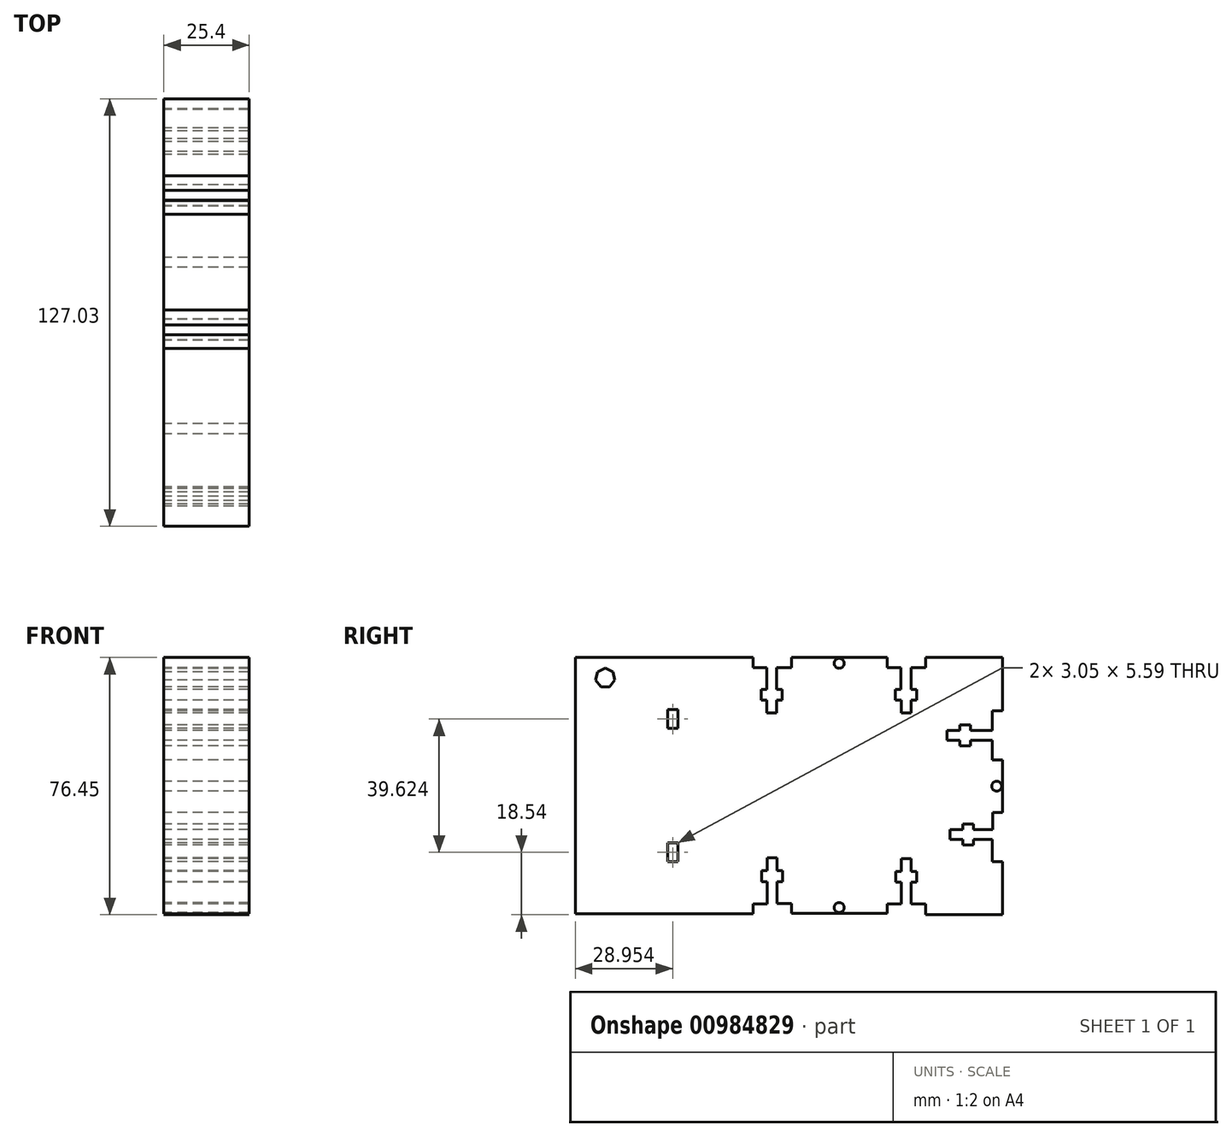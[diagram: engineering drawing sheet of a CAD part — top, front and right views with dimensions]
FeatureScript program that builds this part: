
annotation { "Feature Type Name" : "Feature", "Feature Type Description" : "" }
export const myFeature = defineFeature(function(context is Context, id is Id, definition is map)
    precondition{}
    {
        {
            var Q0;
            Q0=qCreatedBy(makeId("Right.planeOp"),FACE);
            var sketch = newSketch(context, id + "F0", { "sketchPlane" : qUnion([Q0])});
            skArc(sketch, "E0", {"start": v(-22.02, -45.03) * mm, "mid": v(-9.13, -44.74) * mm, "end": v(0.89, -36.62) * mm});
            skArc(sketch, "E1", {"start": v(18.14, -21.03) * mm, "mid": v(8.15, -27.32) * mm, "end": v(0.89, -36.62) * mm});
            skArc(sketch, "E2", {"start": v(21.6, -25.34) * mm, "mid": v(20.26, -22.87) * mm, "end": v(18.14, -21.03) * mm});
            skArc(sketch, "E3", {"start": v(21.6, -25.34) * mm, "mid": v(18.5, -36.07) * mm, "end": v(21.6, -46.8) * mm});
            skArc(sketch, "E4", {"start": v(21.6, -46.8) * mm, "mid": v(41.96, -49.62) * mm, "end": v(61.44, -43.07) * mm});
            skArc(sketch, "E5", {"start": v(68.97, -36.73) * mm, "mid": v(64.12, -38.6) * mm, "end": v(61.44, -43.07) * mm});
            skArc(sketch, "E6", {"start": v(68.97, -36.73) * mm, "mid": v(68.28, -47.93) * mm, "end": v(79.33, -49.9) * mm});
            skArc(sketch, "E7", {"start": v(112.9, -23.55) * mm, "mid": v(92.22, -31.76) * mm, "end": v(79.33, -49.9) * mm});
            skArc(sketch, "E8", {"start": v(112.9, -23.55) * mm, "mid": v(98.28, -43.41) * mm, "end": v(105.37, -67.04) * mm});
            skArc(sketch, "E9", {"start": v(105.37, -67.04) * mm, "mid": v(96.03, -62.92) * mm, "end": v(85.99, -61.04) * mm});
            skArc(sketch, "E10", {"start": v(85.99, -61.04) * mm, "mid": v(69.6, -62.3) * mm, "end": v(54.61, -69.05) * mm});
            skLineSegment(sketch, "E11", {"start": v(54.61, -69.05) * mm, "end": v(-72.39, -69.05) * mm});
            skArc(sketch, "E12", {"start": v(-22.02, -45.03) * mm, "mid": v(-51.84, -45.86) * mm, "end": v(-79.75, -56.4) * mm});
            skArc(sketch, "E13", {"start": v(-79.75, -56.4) * mm, "mid": v(-77, -61.67) * mm, "end": v(-71.28, -63.36) * mm});
            skArc(sketch, "E14", {"start": v(-48.38, -63.36) * mm, "mid": v(-59.83, -63.24) * mm, "end": v(-71.28, -63.36) * mm});
            skArc(sketch, "E15", {"start": v(-72.39, -65.62) * mm, "mid": v(-75.46, -67.33) * mm, "end": v(-72.39, -69.05) * mm});
            skArc(sketch, "E16", {"start": v(-72.39, -65.62) * mm, "mid": v(-60.25, -65.94) * mm, "end": v(-48.38, -63.36) * mm});
            skLineSegment(sketch, "E17", {"start": v(27.48, -78.47) * mm, "end": v(29.13, -78.47) * mm});
            skLineSegment(sketch, "E18", {"start": v(29.13, -78.47) * mm, "end": v(29.13, -81.72) * mm});
            skLineSegment(sketch, "E19", {"start": v(29.13, -81.72) * mm, "end": v(27.48, -81.72) * mm});
            skLineSegment(sketch, "E20", {"start": v(27.48, -81.72) * mm, "end": v(27.48, -85.53) * mm});
            skLineSegment(sketch, "E21", {"start": v(27.48, -85.53) * mm, "end": v(24.53, -85.53) * mm});
            skLineSegment(sketch, "E22", {"start": v(24.53, -85.53) * mm, "end": v(24.53, -81.72) * mm});
            skLineSegment(sketch, "E23", {"start": v(24.43, -72) * mm, "end": v(20.32, -72) * mm});
            skLineSegment(sketch, "E24", {"start": v(-44.9, -69.05) * mm, "end": v(-72.39, -69.05) * mm});
            skLineSegment(sketch, "E25", {"start": v(-72.39, -69.05) * mm, "end": v(-72.39, -145.25) * mm});
            skLineSegment(sketch, "E26", {"start": v(46.05, -123.08) * mm, "end": v(46.05, -124.73) * mm});
            skLineSegment(sketch, "E27", {"start": v(45.19, -95.3) * mm, "end": v(41.94, -95.3) * mm});
            skLineSegment(sketch, "E28", {"start": v(41.94, -95.3) * mm, "end": v(41.94, -93.65) * mm});
            skLineSegment(sketch, "E29", {"start": v(41.94, -93.65) * mm, "end": v(38.13, -93.65) * mm});
            skLineSegment(sketch, "E30", {"start": v(38.13, -93.65) * mm, "end": v(38.13, -90.7) * mm});
            skLineSegment(sketch, "E31", {"start": v(38.13, -90.7) * mm, "end": v(41.94, -90.7) * mm});
            skLineSegment(sketch, "E32", {"start": v(41.94, -90.7) * mm, "end": v(41.94, -89.05) * mm});
            skLineSegment(sketch, "E33", {"start": v(41.94, -89.05) * mm, "end": v(45.19, -89.05) * mm});
            skLineSegment(sketch, "E34", {"start": v(45.19, -89.05) * mm, "end": v(45.19, -90.7) * mm});
            skLineSegment(sketch, "E35", {"start": v(45.19, -90.7) * mm, "end": v(51.67, -90.7) * mm});
            skLineSegment(sketch, "E36", {"start": v(54.64, -115.05) * mm, "end": v(51.7, -115.05) * mm});
            skLineSegment(sketch, "E37", {"start": v(51.7, -115.05) * mm, "end": v(51.7, -120.13) * mm});
            skLineSegment(sketch, "E38", {"start": v(46.05, -120.13) * mm, "end": v(46.05, -118.48) * mm});
            skLineSegment(sketch, "E39", {"start": v(24.43, -72) * mm, "end": v(24.43, -78.47) * mm});
            skLineSegment(sketch, "E40", {"start": v(24.43, -78.47) * mm, "end": v(22.78, -78.47) * mm});
            skLineSegment(sketch, "E41", {"start": v(22.78, -78.47) * mm, "end": v(22.78, -81.72) * mm});
            skLineSegment(sketch, "E42", {"start": v(22.78, -81.72) * mm, "end": v(24.53, -81.72) * mm});
            skLineSegment(sketch, "E43", {"start": v(46.05, -118.48) * mm, "end": v(42.8, -118.48) * mm});
            skLineSegment(sketch, "E44", {"start": v(42.8, -118.48) * mm, "end": v(42.8, -120.13) * mm});
            skLineSegment(sketch, "E45", {"start": v(42.8, -120.13) * mm, "end": v(38.99, -120.13) * mm});
            skLineSegment(sketch, "E46", {"start": v(38.99, -120.13) * mm, "end": v(38.99, -123.08) * mm});
            skLineSegment(sketch, "E47", {"start": v(38.99, -123.08) * mm, "end": v(42.8, -123.08) * mm});
            skLineSegment(sketch, "E48", {"start": v(42.8, -123.08) * mm, "end": v(42.8, -124.73) * mm});
            skLineSegment(sketch, "E49", {"start": v(42.8, -124.73) * mm, "end": v(46.05, -124.73) * mm});
            skLineSegment(sketch, "E50", {"start": v(51.7, -120.13) * mm, "end": v(46.05, -120.13) * mm});
            skLineSegment(sketch, "E51", {"start": v(54.61, -129.68) * mm, "end": v(54.61, -145.5) * mm});
            skLineSegment(sketch, "E52", {"start": v(54.61, -145.5) * mm, "end": v(31.75, -145.5) * mm});
            skLineSegment(sketch, "E53", {"start": v(27.48, -78.47) * mm, "end": v(27.48, -72) * mm});
            skLineSegment(sketch, "E54", {"start": v(27.48, -72) * mm, "end": v(31.75, -72) * mm});
            skLineSegment(sketch, "E55", {"start": v(31.75, -72) * mm, "end": v(31.75, -69.05) * mm});
            skLineSegment(sketch, "E56", {"start": v(31.75, -69.05) * mm, "end": v(54.61, -69.05) * mm});
            skLineSegment(sketch, "E57", {"start": v(54.61, -69.05) * mm, "end": v(54.61, -72) * mm});
            skLineSegment(sketch, "E58", {"start": v(51.67, -84.86) * mm, "end": v(54.61, -84.86) * mm});
            skLineSegment(sketch, "E59", {"start": v(54.61, -84.86) * mm, "end": v(54.61, -72) * mm});
            skLineSegment(sketch, "E60", {"start": v(51.67, -99.48) * mm, "end": v(54.64, -99.48) * mm});
            skLineSegment(sketch, "E61", {"start": v(54.64, -99.48) * mm, "end": v(54.64, -115.05) * mm});
            skLineSegment(sketch, "E62", {"start": v(24.56, -142.32) * mm, "end": v(24.56, -135.84) * mm});
            skLineSegment(sketch, "E63", {"start": v(24.56, -135.84) * mm, "end": v(22.91, -135.84) * mm});
            skLineSegment(sketch, "E64", {"start": v(27.51, -135.84) * mm, "end": v(29.16, -135.84) * mm});
            skLineSegment(sketch, "E65", {"start": v(29.16, -135.84) * mm, "end": v(29.16, -132.59) * mm});
            skLineSegment(sketch, "E66", {"start": v(29.16, -132.59) * mm, "end": v(27.51, -132.59) * mm});
            skLineSegment(sketch, "E67", {"start": v(27.51, -132.59) * mm, "end": v(27.51, -128.78) * mm});
            skLineSegment(sketch, "E68", {"start": v(27.51, -128.78) * mm, "end": v(24.56, -128.78) * mm});
            skLineSegment(sketch, "E69", {"start": v(24.56, -128.78) * mm, "end": v(24.56, -132.59) * mm});
            skLineSegment(sketch, "E70", {"start": v(24.56, -132.59) * mm, "end": v(22.91, -132.59) * mm});
            skLineSegment(sketch, "E71", {"start": v(22.91, -132.59) * mm, "end": v(22.91, -135.84) * mm});
            skLineSegment(sketch, "E72", {"start": v(20.32, -145.07) * mm, "end": v(-8.13, -145.07) * mm});
            skLineSegment(sketch, "E73", {"start": v(-15.31, -135.65) * mm, "end": v(-16.97, -135.65) * mm});
            skLineSegment(sketch, "E74", {"start": v(-12.37, -135.65) * mm, "end": v(-10.72, -135.65) * mm});
            skLineSegment(sketch, "E75", {"start": v(-10.72, -135.65) * mm, "end": v(-10.72, -132.4) * mm});
            skLineSegment(sketch, "E76", {"start": v(-10.72, -132.4) * mm, "end": v(-12.37, -132.4) * mm});
            skLineSegment(sketch, "E77", {"start": v(-12.37, -132.4) * mm, "end": v(-12.37, -128.59) * mm});
            skLineSegment(sketch, "E78", {"start": v(-12.37, -128.59) * mm, "end": v(-15.31, -128.59) * mm});
            skLineSegment(sketch, "E79", {"start": v(-15.31, -128.59) * mm, "end": v(-15.31, -132.4) * mm});
            skLineSegment(sketch, "E80", {"start": v(-15.31, -132.4) * mm, "end": v(-16.97, -132.4) * mm});
            skLineSegment(sketch, "E81", {"start": v(-16.97, -132.4) * mm, "end": v(-16.97, -135.65) * mm});
            skLineSegment(sketch, "E82", {"start": v(-8.13, -142.12) * mm, "end": v(-8.13, -145.07) * mm});
            skLineSegment(sketch, "E83", {"start": v(-72.39, -145.25) * mm, "end": v(-19.56, -145.25) * mm});
            skLineSegment(sketch, "E84", {"start": v(20.32, -72) * mm, "end": v(20.32, -69.05) * mm});
            skLineSegment(sketch, "E85", {"start": v(20.32, -69.05) * mm, "end": v(-8.13, -69.05) * mm});
            skLineSegment(sketch, "E86", {"start": v(-8.13, -72) * mm, "end": v(-12.5, -72) * mm});
            skLineSegment(sketch, "E87", {"start": v(-12.5, -72) * mm, "end": v(-12.5, -78.47) * mm});
            skLineSegment(sketch, "E88", {"start": v(-12.5, -78.47) * mm, "end": v(-10.84, -78.47) * mm});
            skLineSegment(sketch, "E89", {"start": v(-10.84, -78.47) * mm, "end": v(-10.84, -81.72) * mm});
            skLineSegment(sketch, "E90", {"start": v(-10.84, -81.72) * mm, "end": v(-12.5, -81.72) * mm});
            skLineSegment(sketch, "E91", {"start": v(-12.5, -81.72) * mm, "end": v(-12.5, -85.53) * mm});
            skLineSegment(sketch, "E92", {"start": v(-12.5, -85.53) * mm, "end": v(-15.44, -85.53) * mm});
            skLineSegment(sketch, "E93", {"start": v(-15.44, -85.53) * mm, "end": v(-15.44, -81.72) * mm});
            skLineSegment(sketch, "E94", {"start": v(-15.44, -81.72) * mm, "end": v(-17.1, -81.72) * mm});
            skLineSegment(sketch, "E95", {"start": v(-17.1, -81.72) * mm, "end": v(-17.1, -78.47) * mm});
            skLineSegment(sketch, "E96", {"start": v(-17.1, -78.47) * mm, "end": v(-15.44, -78.47) * mm});
            skLineSegment(sketch, "E97", {"start": v(-15.44, -78.47) * mm, "end": v(-15.44, -72) * mm});
            skLineSegment(sketch, "E98", {"start": v(-15.44, -72) * mm, "end": v(-19.56, -72) * mm});
            skLineSegment(sketch, "E99", {"start": v(-19.56, -72) * mm, "end": v(-19.56, -69.05) * mm});
            skLineSegment(sketch, "E100", {"start": v(-8.13, -69.05) * mm, "end": v(-8.13, -72) * mm});
            skLineSegment(sketch, "E101", {"start": v(-44.9, -69.05) * mm, "end": v(-19.56, -69.05) * mm});
            skCircle(sketch, "E102", {"center": v(52.91, -107.27) * mm, "radius": 1.47 * mm});
            skCircle(sketch, "E103", {"center": v(6.1, -143.34) * mm, "radius": 1.47 * mm});
            skPoint(sketch, "E103.centerSnap0", {"position": v(6.1, -145.07) * mm});
            skLineSegment(sketch, "E104", {"start": v(51.64, -129.68) * mm, "end": v(54.61, -129.68) * mm});
            skLineSegment(sketch, "E105", {"start": v(46.05, -123.08) * mm, "end": v(51.65, -123.08) * mm});
            skLineSegment(sketch, "E106", {"start": v(51.65, -123.08) * mm, "end": v(51.64, -129.68) * mm});
            skLineSegment(sketch, "E107", {"start": v(54.61, -69.05) * mm, "end": v(31.75, -69.05) * mm});
            skLineSegment(sketch, "E108", {"start": v(-15.31, -135.65) * mm, "end": v(-15.31, -142.3) * mm});
            skLineSegment(sketch, "E109", {"start": v(-15.31, -142.3) * mm, "end": v(-19.56, -142.3) * mm});
            skLineSegment(sketch, "E110", {"start": v(-19.56, -142.3) * mm, "end": v(-19.56, -145.25) * mm});
            skCircle(sketch, "E111", {"center": v(6.1, -70.77) * mm, "radius": 1.47 * mm});
            skLineSegment(sketch, "E112", {"start": v(24.56, -142.32) * mm, "end": v(20.32, -142.32) * mm});
            skLineSegment(sketch, "E113", {"start": v(20.32, -142.32) * mm, "end": v(20.32, -145.07) * mm});
            skLineSegment(sketch, "E114", {"start": v(27.51, -135.84) * mm, "end": v(27.51, -142.32) * mm});
            skLineSegment(sketch, "E115", {"start": v(27.51, -142.32) * mm, "end": v(31.75, -142.32) * mm});
            skLineSegment(sketch, "E116", {"start": v(31.75, -142.32) * mm, "end": v(31.75, -145.5) * mm});
            skLineSegment(sketch, "E117", {"start": v(-12.37, -135.65) * mm, "end": v(-12.37, -142.12) * mm});
            skLineSegment(sketch, "E118", {"start": v(-12.37, -142.12) * mm, "end": v(-8.13, -142.12) * mm});
            skLineSegment(sketch, "E119", {"start": v(45.19, -95.3) * mm, "end": v(45.19, -93.64) * mm});
            skLineSegment(sketch, "E120", {"start": v(45.19, -93.64) * mm, "end": v(51.67, -93.64) * mm});
            skLineSegment(sketch, "E121", {"start": v(51.67, -93.64) * mm, "end": v(51.67, -99.48) * mm});
            skLineSegment(sketch, "E122", {"start": v(51.67, -90.7) * mm, "end": v(51.67, -84.86) * mm});
            skCircle(sketch, "E123.cCircle", {"center": v(-63.5, -75.11) * mm, "radius": 2.65 * mm, "construction": true});
            skLineSegment(sketch, "E123.0", {"start": v(-62.22, -77.77) * mm, "end": v(-64.77, -77.77) * mm});
            skLineSegment(sketch, "E123.1", {"start": v(-64.77, -77.77) * mm, "end": v(-66.36, -75.77) * mm});
            skLineSegment(sketch, "E123.2", {"start": v(-66.36, -75.77) * mm, "end": v(-65.8, -73.28) * mm});
            skLineSegment(sketch, "E123.3", {"start": v(-65.8, -73.28) * mm, "end": v(-63.5, -72.17) * mm});
            skLineSegment(sketch, "E123.4", {"start": v(-63.5, -72.17) * mm, "end": v(-61.2, -73.28) * mm});
            skLineSegment(sketch, "E123.5", {"start": v(-61.2, -73.28) * mm, "end": v(-60.62, -75.77) * mm});
            skLineSegment(sketch, "E123.6", {"start": v(-60.62, -75.77) * mm, "end": v(-62.22, -77.77) * mm});
            skPoint(sketch, "E123.0.midPoint", {"position": v(-63.5, -77.77) * mm});
            skLineSegment(sketch, "E124.bottom", {"start": v(-41.9, -84.54) * mm, "end": v(-41.9, -90.13) * mm});
            skLineSegment(sketch, "E124.top", {"start": v(-44.96, -84.54) * mm, "end": v(-44.96, -90.13) * mm});
            skLineSegment(sketch, "E124.left", {"start": v(-41.9, -84.54) * mm, "end": v(-44.96, -84.54) * mm});
            skLineSegment(sketch, "E124.right", {"start": v(-41.9, -90.13) * mm, "end": v(-44.96, -90.13) * mm});
            skLineSegment(sketch, "E125.MirrorCS", {"start": v(-41.9, -129.75) * mm, "end": v(-44.96, -129.75) * mm});
            skLineSegment(sketch, "E126.MirrorCS", {"start": v(-44.96, -129.75) * mm, "end": v(-44.96, -124.16) * mm});
            skLineSegment(sketch, "E127.MirrorCS", {"start": v(-41.9, -129.75) * mm, "end": v(-41.9, -124.16) * mm});
            skLineSegment(sketch, "E128.MirrorCS", {"start": v(-41.9, -124.16) * mm, "end": v(-44.96, -124.16) * mm});
            skSolve(sketch);
        }
        {
            var Q0;
            Q0=makeQuery(id+"F0.imprint","IMPRINT",FACE,{"disambiguationData":[TD([[makeQuery(id+"F0.imprint","IMPRINT",EDGE,{"derivedFrom":sQuery(id+"F0.wireOp",EDGE,"E17")}),1.0]])]});
            extrude(context, id + "F1", {"entities" : qUnion([Q0]), "depth" : 25.4 * mm, "offsetDistance" : 25.4 * mm});
        }
        {
            var Q0;
            Q0=makeQuery(id+"F1.opExtrude","SWEPT_BODY",BODY,{"disambiguationData":[OSD([sQuery(id+"F0.wireOp",EDGE,"E17"),sQuery(id+"F0.wireOp",EDGE,"E18"),sQuery(id+"F0.wireOp",EDGE,"E19"),sQuery(id+"F0.wireOp",EDGE,"E20"),sQuery(id+"F0.wireOp",EDGE,"E21"),sQuery(id+"F0.wireOp",EDGE,"E22"),sQuery(id+"F0.wireOp",EDGE,"E23"),sQuery(id+"F0.wireOp",EDGE,"E24"),sQuery(id+"F0.wireOp",EDGE,"E25"),sQuery(id+"F0.wireOp",EDGE,"E26"),sQuery(id+"F0.wireOp",EDGE,"E27"),sQuery(id+"F0.wireOp",EDGE,"E28"),sQuery(id+"F0.wireOp",EDGE,"E29"),sQuery(id+"F0.wireOp",EDGE,"E30"),sQuery(id+"F0.wireOp",EDGE,"E31"),sQuery(id+"F0.wireOp",EDGE,"E32"),sQuery(id+"F0.wireOp",EDGE,"E33"),sQuery(id+"F0.wireOp",EDGE,"E34"),sQuery(id+"F0.wireOp",EDGE,"E35"),sQuery(id+"F0.wireOp",EDGE,"E36"),sQuery(id+"F0.wireOp",EDGE,"E37"),sQuery(id+"F0.wireOp",EDGE,"E38"),sQuery(id+"F0.wireOp",EDGE,"E39"),sQuery(id+"F0.wireOp",EDGE,"E40"),sQuery(id+"F0.wireOp",EDGE,"E41"),sQuery(id+"F0.wireOp",EDGE,"E42"),sQuery(id+"F0.wireOp",EDGE,"E43"),sQuery(id+"F0.wireOp",EDGE,"E44"),sQuery(id+"F0.wireOp",EDGE,"E45"),sQuery(id+"F0.wireOp",EDGE,"E46"),sQuery(id+"F0.wireOp",EDGE,"E47"),sQuery(id+"F0.wireOp",EDGE,"E48"),sQuery(id+"F0.wireOp",EDGE,"E49"),sQuery(id+"F0.wireOp",EDGE,"E50"),sQuery(id+"F0.wireOp",EDGE,"E51"),sQuery(id+"F0.wireOp",EDGE,"E52"),sQuery(id+"F0.wireOp",EDGE,"E53"),sQuery(id+"F0.wireOp",EDGE,"E54"),sQuery(id+"F0.wireOp",EDGE,"E55"),sQuery(id+"F0.wireOp",EDGE,"E57"),sQuery(id+"F0.wireOp",EDGE,"E58"),sQuery(id+"F0.wireOp",EDGE,"E59"),sQuery(id+"F0.wireOp",EDGE,"E60"),sQuery(id+"F0.wireOp",EDGE,"E61"),sQuery(id+"F0.wireOp",EDGE,"E62"),sQuery(id+"F0.wireOp",EDGE,"E63"),sQuery(id+"F0.wireOp",EDGE,"E64"),sQuery(id+"F0.wireOp",EDGE,"E65"),sQuery(id+"F0.wireOp",EDGE,"E66"),sQuery(id+"F0.wireOp",EDGE,"E67"),sQuery(id+"F0.wireOp",EDGE,"E68"),sQuery(id+"F0.wireOp",EDGE,"E69"),sQuery(id+"F0.wireOp",EDGE,"E70"),sQuery(id+"F0.wireOp",EDGE,"E71"),sQuery(id+"F0.wireOp",EDGE,"E72"),sQuery(id+"F0.wireOp",EDGE,"E73"),sQuery(id+"F0.wireOp",EDGE,"E74"),sQuery(id+"F0.wireOp",EDGE,"E75"),sQuery(id+"F0.wireOp",EDGE,"E76"),sQuery(id+"F0.wireOp",EDGE,"E77"),sQuery(id+"F0.wireOp",EDGE,"E78"),sQuery(id+"F0.wireOp",EDGE,"E79"),sQuery(id+"F0.wireOp",EDGE,"E80"),sQuery(id+"F0.wireOp",EDGE,"E81"),sQuery(id+"F0.wireOp",EDGE,"E82"),sQuery(id+"F0.wireOp",EDGE,"E83"),sQuery(id+"F0.wireOp",EDGE,"E84"),sQuery(id+"F0.wireOp",EDGE,"E85"),sQuery(id+"F0.wireOp",EDGE,"E86"),sQuery(id+"F0.wireOp",EDGE,"E87"),sQuery(id+"F0.wireOp",EDGE,"E88"),sQuery(id+"F0.wireOp",EDGE,"E89"),sQuery(id+"F0.wireOp",EDGE,"E90"),sQuery(id+"F0.wireOp",EDGE,"E91"),sQuery(id+"F0.wireOp",EDGE,"E92"),sQuery(id+"F0.wireOp",EDGE,"E93"),sQuery(id+"F0.wireOp",EDGE,"E94"),sQuery(id+"F0.wireOp",EDGE,"E95"),sQuery(id+"F0.wireOp",EDGE,"E96"),sQuery(id+"F0.wireOp",EDGE,"E97"),sQuery(id+"F0.wireOp",EDGE,"E98"),sQuery(id+"F0.wireOp",EDGE,"E99"),sQuery(id+"F0.wireOp",EDGE,"E100"),sQuery(id+"F0.wireOp",EDGE,"E101"),sQuery(id+"F0.wireOp",EDGE,"E102"),sQuery(id+"F0.wireOp",EDGE,"E103"),sQuery(id+"F0.wireOp",EDGE,"E104"),sQuery(id+"F0.wireOp",EDGE,"E105"),sQuery(id+"F0.wireOp",EDGE,"E106"),sQuery(id+"F0.wireOp",EDGE,"E107"),sQuery(id+"F0.wireOp",EDGE,"E108"),sQuery(id+"F0.wireOp",EDGE,"E109"),sQuery(id+"F0.wireOp",EDGE,"E110"),sQuery(id+"F0.wireOp",EDGE,"E111"),sQuery(id+"F0.wireOp",EDGE,"E112"),sQuery(id+"F0.wireOp",EDGE,"E113"),sQuery(id+"F0.wireOp",EDGE,"E114"),sQuery(id+"F0.wireOp",EDGE,"E115"),sQuery(id+"F0.wireOp",EDGE,"E116"),sQuery(id+"F0.wireOp",EDGE,"E117"),sQuery(id+"F0.wireOp",EDGE,"E118"),sQuery(id+"F0.wireOp",EDGE,"E119"),sQuery(id+"F0.wireOp",EDGE,"E120"),sQuery(id+"F0.wireOp",EDGE,"E121"),sQuery(id+"F0.wireOp",EDGE,"E122"),sQuery(id+"F0.wireOp",EDGE,"E123.0"),sQuery(id+"F0.wireOp",EDGE,"E123.1"),sQuery(id+"F0.wireOp",EDGE,"E123.2"),sQuery(id+"F0.wireOp",EDGE,"E123.3"),sQuery(id+"F0.wireOp",EDGE,"E123.4"),sQuery(id+"F0.wireOp",EDGE,"E123.5"),sQuery(id+"F0.wireOp",EDGE,"E123.6"),sQuery(id+"F0.wireOp",EDGE,"E124.bottom"),sQuery(id+"F0.wireOp",EDGE,"E124.top"),sQuery(id+"F0.wireOp",EDGE,"E124.left"),sQuery(id+"F0.wireOp",EDGE,"E124.right"),sQuery(id+"F0.wireOp",EDGE,"E125.MirrorCS"),sQuery(id+"F0.wireOp",EDGE,"E126.MirrorCS"),sQuery(id+"F0.wireOp",EDGE,"E127.MirrorCS"),sQuery(id+"F0.wireOp",EDGE,"E128.MirrorCS")])]});
            transform(context, id + "F2", {"entities" : qUnion([Q0]), "transformType" : TransformType.TRANSLATION_3D, "dx" : 0 * mm, "dy" : -1.52 * mm, "dz" : -27.43 * mm, "makeCopy" : false});
        }
    });
